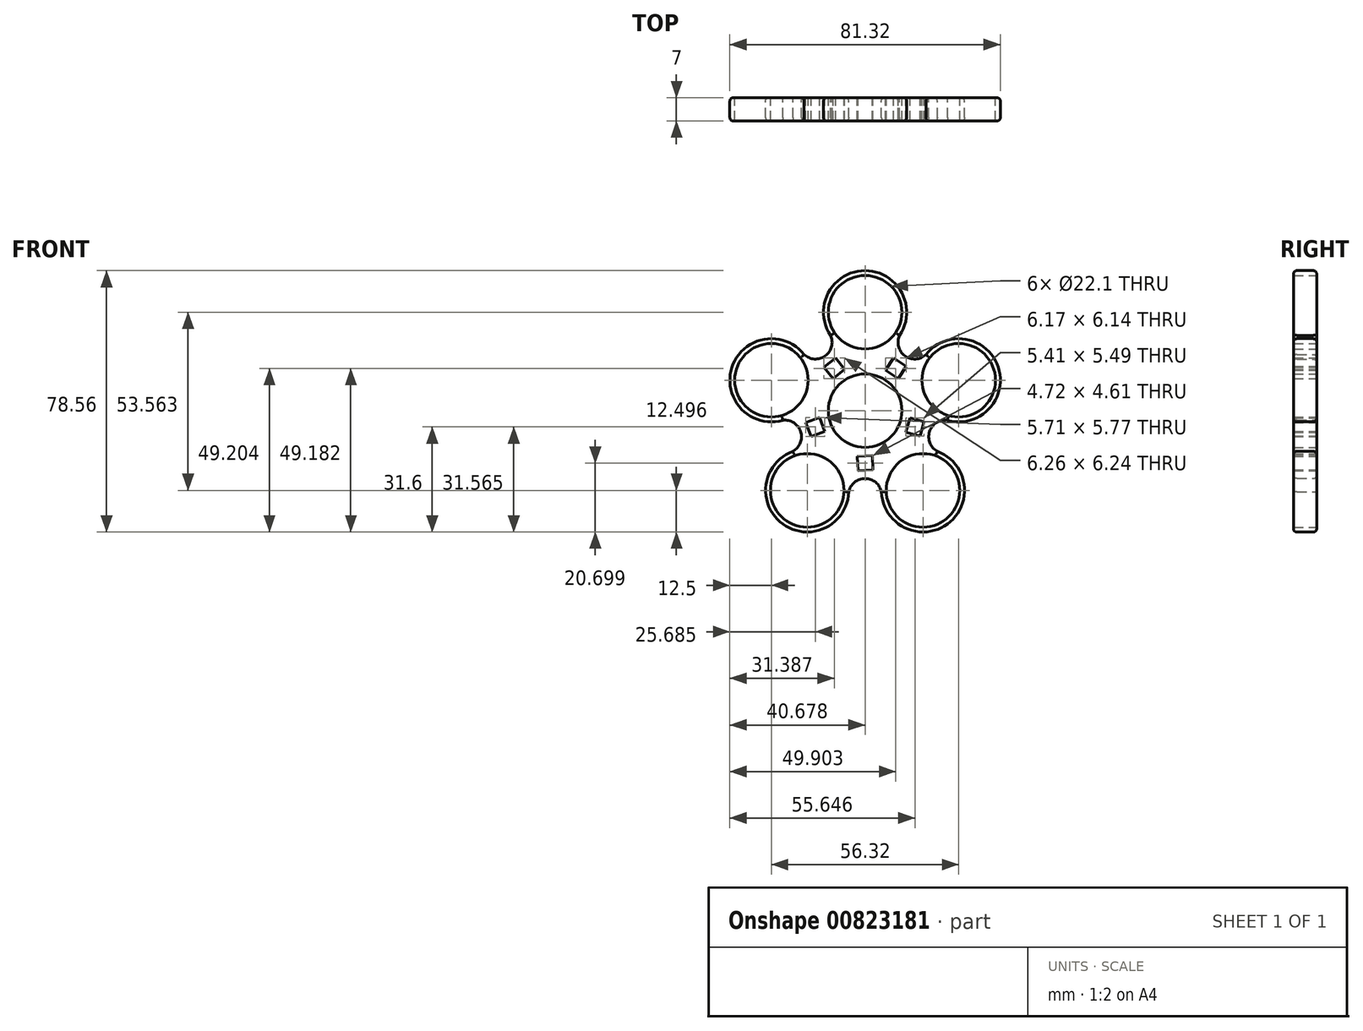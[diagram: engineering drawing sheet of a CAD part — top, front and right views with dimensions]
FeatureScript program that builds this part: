
annotation { "Feature Type Name" : "Feature", "Feature Type Description" : "" }
export const myFeature = defineFeature(function(context is Context, id is Id, definition is map)
    precondition{}
    {
        {
            var Q0;
            Q0=qCreatedBy(makeId("Front.planeOp"),FACE);
            var sketch = newSketch(context, id + "F0", { "sketchPlane" : qUnion([Q0])});
            skCircle(sketch, "E0", {"center": v(0, 0) * mm, "radius": 11.05 * mm});
            skCircle(sketch, "E1", {"center": v(0, 0) * mm, "radius": 12.5 * mm});
            skCircle(sketch, "E2", {"center": v(0, 29.6) * mm, "radius": 11.05 * mm});
            skCircle(sketch, "E3", {"center": v(0, 29.6) * mm, "radius": 12.5 * mm});
            skCircle(sketch, "E4.1.0", {"center": v(-28.16, 9.15) * mm, "radius": 12.5 * mm});
            skCircle(sketch, "E4.1.1", {"center": v(-28.16, 9.15) * mm, "radius": 11.05 * mm});
            skCircle(sketch, "E4.2.0", {"center": v(-17.4, -23.95) * mm, "radius": 12.5 * mm});
            skCircle(sketch, "E4.2.1", {"center": v(-17.4, -23.95) * mm, "radius": 11.05 * mm});
            skCircle(sketch, "E4.3.0", {"center": v(17.4, -23.95) * mm, "radius": 12.5 * mm});
            skCircle(sketch, "E4.3.1", {"center": v(17.4, -23.95) * mm, "radius": 11.05 * mm});
            skCircle(sketch, "E4.4.0", {"center": v(28.16, 9.15) * mm, "radius": 12.5 * mm});
            skCircle(sketch, "E4.4.1", {"center": v(28.16, 9.15) * mm, "radius": 11.05 * mm});
            skArc(sketch, "E5", {"start": v(10.4, 22.66) * mm, "mid": v(11.97, 16.5) * mm, "end": v(18.33, 16.87) * mm});
            skArc(sketch, "E6.1.0", {"start": v(-18.34, 16.89) * mm, "mid": v(-11.98, 16.48) * mm, "end": v(-10.38, 22.65) * mm});
            skArc(sketch, "E6.2.0", {"start": v(-21.73, -12.23) * mm, "mid": v(-19.38, -6.3) * mm, "end": v(-24.75, -2.88) * mm});
            skArc(sketch, "E6.3.0", {"start": v(4.91, -24.44) * mm, "mid": v(0, -20.38) * mm, "end": v(-4.91, -24.43) * mm});
            skArc(sketch, "E6.4.0", {"start": v(24.77, -2.88) * mm, "mid": v(19.38, -6.29) * mm, "end": v(21.71, -12.22) * mm});
            skSolve(sketch);
        }
        {
            var Q0;
            Q0 = qSketchRegion(id + "F0", true);
            var Q1;
            Q1=makeQuery(id+"F0.imprint","IMPRINT",FACE,{"disambiguationData":[TD([[makeQuery(id+"F0.imprint","IMPRINT",EDGE,{"derivedFrom":sQuery(id+"F0.wireOp",EDGE,"E1")}),1.0]])]});
            extrude(context, id + "F1", {"entities" : qUnion([Q0, Q1]), "depth" : 7 * mm, "offsetDistance" : 25 * mm});
        }
        {
            var Q0;
            Q0=qCreatedBy(makeId("Front.planeOp"),FACE);
            var sketch = newSketch(context, id + "F2", { "sketchPlane" : qUnion([Q0])});
            skLineSegment(sketch, "E7.0", {"start": v(-8.9, 15.85) * mm, "end": v(-6.14, 12.44) * mm});
            skLineSegment(sketch, "E7.1", {"start": v(-6.14, 12.44) * mm, "end": v(-9.65, 9.61) * mm});
            skLineSegment(sketch, "E7.2", {"start": v(-9.65, 9.61) * mm, "end": v(-12.4, 13.02) * mm});
            skLineSegment(sketch, "E7.3", {"start": v(-12.4, 13.02) * mm, "end": v(-8.9, 15.85) * mm});
            skPoint(sketch, "E7.0.midPoint", {"position": v(-7.52, 14.15) * mm});
            skLineSegment(sketch, "E8.1.0", {"start": v(-16.22, -7.77) * mm, "end": v(-17.83, -3.57) * mm});
            skLineSegment(sketch, "E8.1.1", {"start": v(-12.12, -6.2) * mm, "end": v(-16.22, -7.77) * mm});
            skLineSegment(sketch, "E8.1.2", {"start": v(-13.73, -2) * mm, "end": v(-12.12, -6.2) * mm});
            skLineSegment(sketch, "E8.1.3", {"start": v(-17.83, -3.57) * mm, "end": v(-13.73, -2) * mm});
            skLineSegment(sketch, "E8.2.0", {"start": v(2.38, -17.83) * mm, "end": v(-2.12, -18.06) * mm});
            skLineSegment(sketch, "E8.2.1", {"start": v(2.15, -13.44) * mm, "end": v(2.38, -17.83) * mm});
            skLineSegment(sketch, "E8.2.2", {"start": v(-2.34, -13.67) * mm, "end": v(2.15, -13.44) * mm});
            skLineSegment(sketch, "E8.2.3", {"start": v(-2.12, -18.06) * mm, "end": v(-2.34, -13.67) * mm});
            skLineSegment(sketch, "E8.3.0", {"start": v(17.7, -3.25) * mm, "end": v(16.52, -7.6) * mm});
            skLineSegment(sketch, "E8.3.1", {"start": v(13.45, -2.1) * mm, "end": v(17.7, -3.25) * mm});
            skLineSegment(sketch, "E8.3.2", {"start": v(12.28, -6.45) * mm, "end": v(13.45, -2.1) * mm});
            skLineSegment(sketch, "E8.3.3", {"start": v(16.52, -7.6) * mm, "end": v(12.28, -6.45) * mm});
            skLineSegment(sketch, "E8.4.0", {"start": v(8.55, 15.82) * mm, "end": v(12.33, 13.36) * mm});
            skLineSegment(sketch, "E8.4.1", {"start": v(6.16, 12.14) * mm, "end": v(8.55, 15.82) * mm});
            skLineSegment(sketch, "E8.4.2", {"start": v(9.93, 9.69) * mm, "end": v(6.16, 12.14) * mm});
            skLineSegment(sketch, "E8.4.3", {"start": v(12.33, 13.36) * mm, "end": v(9.93, 9.69) * mm});
            skPoint(sketch, "E8.center", {"position": v(0, 0) * mm});
            skSolve(sketch);
        }
        {
            var Q0;
            Q0 = qSketchRegion(id + "F2", true);
            extrude(context, id + "F3", {"entities" : qUnion([Q0]), "operationType" : NewBodyOperationType.REMOVE, "oppositeDirection" : true, "depth" : -7 * mm, "offsetDistance" : 25 * mm});
        }
        {
            var Q0;
            Q0=makeQuery(id+"F1.opExtrude","CAP_EDGE",EDGE,{"disambiguationData":[OSD([sQuery(id+"F0.wireOp",EDGE,"E4.1.0")])],"isStart":false});
            var Q1;
            Q1=makeQuery(id+"F1.opExtrude","CAP_EDGE",EDGE,{"disambiguationData":[OSD([sQuery(id+"F0.wireOp",EDGE,"E6.1.0")])],"isStart":false});
            var Q2;
            Q2=makeQuery(id+"F1.opExtrude","CAP_EDGE",EDGE,{"disambiguationData":[OSD([sQuery(id+"F0.wireOp",EDGE,"E3")])],"isStart":false});
            var Q3;
            Q3=makeQuery(id+"F1.opExtrude","CAP_EDGE",EDGE,{"disambiguationData":[OSD([sQuery(id+"F0.wireOp",EDGE,"E5")])],"isStart":false});
            var Q4;
            Q4=makeQuery(id+"F1.opExtrude","CAP_EDGE",EDGE,{"disambiguationData":[OSD([sQuery(id+"F0.wireOp",EDGE,"E4.4.0")])],"isStart":false});
            var Q5;
            Q5=makeQuery(id+"F1.opExtrude","CAP_EDGE",EDGE,{"disambiguationData":[OSD([sQuery(id+"F0.wireOp",EDGE,"E6.4.0")])],"isStart":false});
            var Q6;
            Q6=makeQuery(id+"F1.opExtrude","CAP_EDGE",EDGE,{"disambiguationData":[OSD([sQuery(id+"F0.wireOp",EDGE,"E4.3.0")])],"isStart":false});
            var Q7;
            Q7=makeQuery(id+"F1.opExtrude","CAP_EDGE",EDGE,{"disambiguationData":[OSD([sQuery(id+"F0.wireOp",EDGE,"E6.3.0")])],"isStart":false});
            var Q8;
            Q8=makeQuery(id+"F1.opExtrude","CAP_EDGE",EDGE,{"disambiguationData":[OSD([sQuery(id+"F0.wireOp",EDGE,"E4.2.0")])],"isStart":false});
            var Q9;
            Q9=makeQuery(id+"F1.opExtrude","CAP_EDGE",EDGE,{"disambiguationData":[OSD([sQuery(id+"F0.wireOp",EDGE,"E6.2.0")])],"isStart":false});
            var Q10;
            Q10=makeQuery(id+"F1.opExtrude","CAP_EDGE",EDGE,{"disambiguationData":[OSD([sQuery(id+"F0.wireOp",EDGE,"E4.3.0")])],"isStart":true});
            var Q11;
            Q11=makeQuery(id+"F1.opExtrude","CAP_EDGE",EDGE,{"disambiguationData":[OSD([sQuery(id+"F0.wireOp",EDGE,"E6.4.0")])],"isStart":true});
            var Q12;
            Q12=makeQuery(id+"F1.opExtrude","CAP_EDGE",EDGE,{"disambiguationData":[OSD([sQuery(id+"F0.wireOp",EDGE,"E5")])],"isStart":true});
            var Q13;
            Q13=makeQuery(id+"F1.opExtrude","CAP_EDGE",EDGE,{"disambiguationData":[OSD([sQuery(id+"F0.wireOp",EDGE,"E3")])],"isStart":true});
            var Q14;
            Q14=makeQuery(id+"F1.opExtrude","CAP_EDGE",EDGE,{"disambiguationData":[OSD([sQuery(id+"F0.wireOp",EDGE,"E4.4.0")])],"isStart":true});
            var Q15;
            Q15=makeQuery(id+"F1.opExtrude","CAP_EDGE",EDGE,{"disambiguationData":[OSD([sQuery(id+"F0.wireOp",EDGE,"E6.1.0")])],"isStart":true});
            var Q16;
            Q16=makeQuery(id+"F1.opExtrude","CAP_EDGE",EDGE,{"disambiguationData":[OSD([sQuery(id+"F0.wireOp",EDGE,"E4.1.0")])],"isStart":true});
            var Q17;
            Q17=makeQuery(id+"F1.opExtrude","CAP_EDGE",EDGE,{"disambiguationData":[OSD([sQuery(id+"F0.wireOp",EDGE,"E6.2.0")])],"isStart":true});
            var Q18;
            Q18=makeQuery(id+"F1.opExtrude","CAP_EDGE",EDGE,{"disambiguationData":[OSD([sQuery(id+"F0.wireOp",EDGE,"E4.2.0")])],"isStart":true});
            var Q19;
            Q19=makeQuery(id+"F1.opExtrude","CAP_EDGE",EDGE,{"disambiguationData":[OSD([sQuery(id+"F0.wireOp",EDGE,"E6.3.0")])],"isStart":true});
            fillet(context, id + "F4", {"entities" : qUnion([Q0, Q1, Q2, Q3, Q4, Q5, Q6, Q7, Q8, Q9, Q10, Q11, Q12, Q13, Q14, Q15, Q16, Q17, Q18, Q19]), "radius" : 1 * mm, "tangentPropagation" : true, "allowEdgeOverflow" : false});
        }
    });
